# Revit family: Haworth_ComposeConnections_Leg
name_source: partatom
category: Furniture Systems
revit_build: Autodesk Revit 2018 (Build: 20170223_1515(x64)
units: mm (PartAtom-declared; Revit-internal decimal feet)

## family parameters
Always vertical = Yes
Cut with Voids When Loaded = No
OmniClass Number = 23.40.70.14.64.21
OmniClass Title = Systems Furniture
Part Type = Normal
Room Calculation Point = No
Round Connector Dimension = Use Diameter
Shared = No
Work Plane-Based = No

## types (1)
- Leg
    Actual Depth = 20"
    Actual Height = 1/4"
    Actual Width = 3"
    Assembly Code = E2020200
    Description = Haworth - Compose Connections - Leg
    Manufacturer = Haworth
    Min/Max Height = 26-32 in.
    Model = VZLL-0800
    Revision Number = 3
    Size = Verify Final Dim. w/ Haworth
    Standard Depths = 12, 18, 24, 30 in.
    Support Finish = Haworth _ Paint _ Gray Tone
    Sustainability Info = http://media.haworth.com
    URL = http://www.haworth.com
    URL - Product = http://www.haworth.com
    Warranty = https://www.haworth.com

## geometry (parser evidence)
native form markers: Sweep x5
no freeform markers — native parametric forms only
